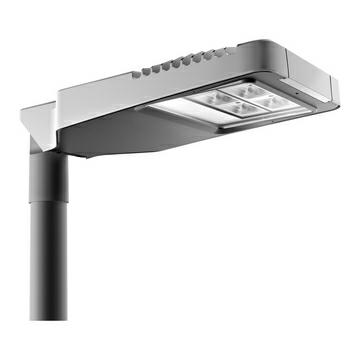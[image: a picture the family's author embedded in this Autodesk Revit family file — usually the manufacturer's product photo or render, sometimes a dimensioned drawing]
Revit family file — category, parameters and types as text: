
# Revit family: Lighting-Stradale-GEWISS-ROAD[5]MEDIUM-LED_OTTICA_HUGE_CLI
name_source: partatom
category: Apparecchi per illuminazione
units: mm (PartAtom-declared; Revit-internal decimal feet)

## family parameters
Basato su piano di lavoro = No
Condiviso = No
Punto di calcolo locali = No
Quota connettore circolare = Usa diametro
Sempre verticale = Sì
Sorgente d'illuminazione = No
Taglio con vuoti quando caricato = No
Tipo di parte = Normale

## types (1)
- Lighting-Stradale-GEWISS-ROAD[5]MEDIUM-LED_OTTICA_HUGE_CLI
    Alimentatore = Incluso
    Apparecchio a ridotta temperatura superficiale = -
    Applicazione = Esterno
    Cablaggio = Sezionatore
    Caratteristiche elettriche e gestione della luce = -
    Caratteristiche ottiche e illuminotecniche = -
    Catalogo = LIGHTING
    Catalogo Serie = ROAD [5]
    Certificazione DIN 18032-3 = -
    Certificazioni e classificazioni = -
    Classe fotobiologica = RG0
    Classe isolamento = I
    Classificazione: = -
    Codice Electrocod = 244C
    Codice digitale univoco (Datamatrix) = Attualmente non presente
    Colore = Grigio grafite
    Contesto = Illuminazione stradale e parcheggi
    Controllo abbagliamento e luminanza = G*3 - ULOR = 0
    Corpo = Alluminio pressofuso
    Corrente di pilotaggio. = 0,7A
    Descrizione = GWR5676M30K - ROAD5 MEDI HUGE 6M 3000K 0,7A CL1 1-10V
    Dispositivo di protezione = DM 10KV / CM 10KV
    Distanza minima dall'oggetto illuminato = 1M
    Durata di vita = L90B10 (Tq+25°C) = 100.000 h - L90B10 (Tq+50°C) = 50.000 h
    Efficienza luminosa (lm/W) = 97
    Finitura colore = Verniciato a polveri
    Fissaggio = Testa palo - Sbraccio
    Flusso nominale (lm) = 16200
    Frequenza nominale (Hz) = 50 / 60
    Funzionalità alimentatore = Dimmerabile
    Gancio di chiusura = Maniglia frontale integrata
    Garanzia = 5 anni
    Grado di protezione = IP66
    Gruppo ottico = Riflettore in PC metallizzato
    Guarnizioni = silicone antinvecchiamento
    IDF = 5ab80f50-71b5-4740-b099-52fe9a9f2aad
    IDT = 9a00d1bcfceb457b92ad59b7f4a86d78
    IPEA = STRADALE = B // GRANDI AREE = A++ // CICLOPEDONALI = A // AREE VERDI = A // CENTRO STORICO = A3+
    Immagine tipo = GWR5276M.jpg
    Inclinazione = -20° ÷ +10° sbraccio - -10° ÷ +20° testa palo
    Indice di resa cromatica = CRI-70
    Informazioni generali = -
    Installazione e manutenzione = -
    LED Life Time (L80B05) = 77000H
    Lampada = LED
    Lampada: = LED
    Lumen output (lm) = 15600
    Materiali = -
    Modello = GWR5676M30K
    Norma di riferimento = EN 60598-2-3, EN 60598-1 IEC/TR 62778
    Numero moduli = 6 (6x3 LED)
    Ottica = HUGE
    Peso (kg): = 9,09999999999999
    Potenza assorbita : = 161 W @ 0.7A
    Potenza di sistema = 159W
    Produttore = GEWISS S.p.A.
    Regolazione inclinazione = -20° ÷ +10° sbraccio - -10° ÷ +20° testa palo
    Resistenza agli urti = IK08
    Resistenza al filo incandescente = -
    Resistenza alle sovratensioni : = 10 KV in modalità comune e differenziale
    SEO = Stradale
    Scheda Tecnica = https://www.gewiss.com
    Schermo = Vetro piano temperato spessore 4mm
    Sistema di controllo = Dimmerabile 1-10 V
    Sostituibilità gruppo ottico = Non disponibile
    Sostituibilità piastra di cablaggio = Non disponibile
    Superficie massima esposta al vento = 0,19M2
    Superficie massima esposta al vento : = 0.19 m2
    Temperatura di colore = 3000K
    Temperatura di colore: = 3000 K (CRI>80)
    Temperatura di esercizio = -25 +50 °C
    Temperatura di stoccaggio = -
    Temperatura di utilizzo = -25 +50 °C
    Tensione = 220/240 V - 50/60 Hz - Dimmerabile 1-10 V
    Tensione di alimentazione = 220 - 240 V
    Tipo alimentatore = Driver Led in corrente continua
    Tipo di apparecchio = Apparecchiatura stradale a LED
    Tipo di installazione e montaggio = Testa palo - Sbraccio
    Tipologia = Dimmerabile
    Tipologia sorgente luminosa = LED - Non sostituibile
    Tolleranza cromatica = SDCM = 5
    URL = https://www.gewiss.com
    Vano di alimentazione = Integrato
    Versione file RFA = 20.11
    Viti esterne = Acciaio inox

## geometry (parser evidence)
native form markers: Blend x2
no freeform markers — native parametric forms only
